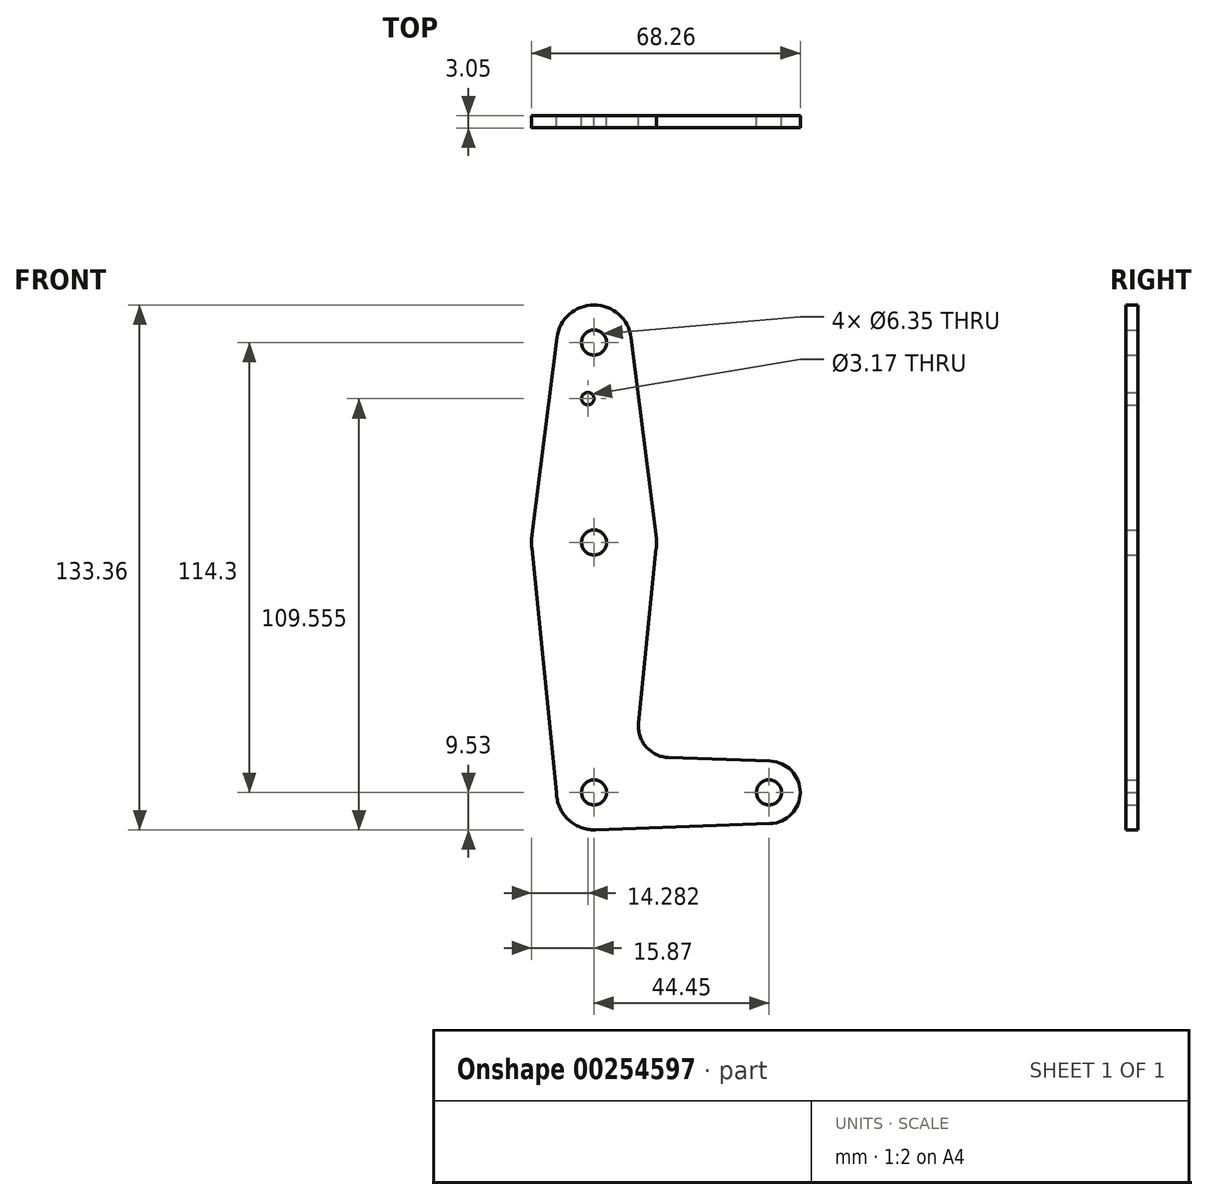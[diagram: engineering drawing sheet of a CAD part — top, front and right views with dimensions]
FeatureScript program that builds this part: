
annotation { "Feature Type Name" : "Feature", "Feature Type Description" : "" }
export const myFeature = defineFeature(function(context is Context, id is Id, definition is map)
    precondition{}
    {
        {
            var Q0;
            Q0=qCreatedBy(makeId("Front.planeOp"),FACE);
            var sketch = newSketch(context, id + "F0", { "sketchPlane" : qUnion([Q0])});
            skCircle(sketch, "E0", {"center": v(0, 0) * mm, "radius": 9.53 * mm});
            skCircle(sketch, "E1", {"center": v(44.45, 0) * mm, "radius": 7.94 * mm});
            skCircle(sketch, "E2", {"center": v(0, 63.5) * mm, "radius": 15.88 * mm});
            skCircle(sketch, "E3", {"center": v(0, 114.3) * mm, "radius": 9.53 * mm});
            skLineSegment(sketch, "E4", {"start": v(44.73, 7.93) * mm, "end": v(18.93, 8.85) * mm});
            skLineSegment(sketch, "E5", {"start": v(44.73, -7.93) * mm, "end": v(0, -9.53) * mm});
            skLineSegment(sketch, "E6", {"start": v(11.3, 17.6) * mm, "end": v(15.8, 61.9) * mm});
            skLineSegment(sketch, "E7", {"start": v(-9.53, 0) * mm, "end": v(-15.8, 61.9) * mm});
            skLineSegment(sketch, "E8", {"start": v(-9.45, 115.5) * mm, "end": v(-15.75, 65.48) * mm});
            skLineSegment(sketch, "E9", {"start": v(9.45, 115.5) * mm, "end": v(15.8, 65.14) * mm});
            skCircle(sketch, "E10", {"center": v(-1.59, 100.03) * mm, "radius": 1.59 * mm});
            skCircle(sketch, "E11", {"center": v(0, 114.3) * mm, "radius": 3.18 * mm});
            skCircle(sketch, "E12", {"center": v(44.45, 0) * mm, "radius": 3.18 * mm});
            skCircle(sketch, "E13", {"center": v(0, 0) * mm, "radius": 3.18 * mm});
            skCircle(sketch, "E14", {"center": v(0, 63.5) * mm, "radius": 3.18 * mm});
            skArc(sketch, "E15.filletArc", {"start": v(11.3, 17.6) * mm, "mid": v(13.22, 11.57) * mm, "end": v(18.93, 8.85) * mm});
            skSolve(sketch);
        }
        {
            var Q0;
            Q0 = qSketchRegion(id + "F0", true);
            extrude(context, id + "F1", {"entities" : qUnion([Q0]), "depth" : 3.05 * mm});
        }
    });
